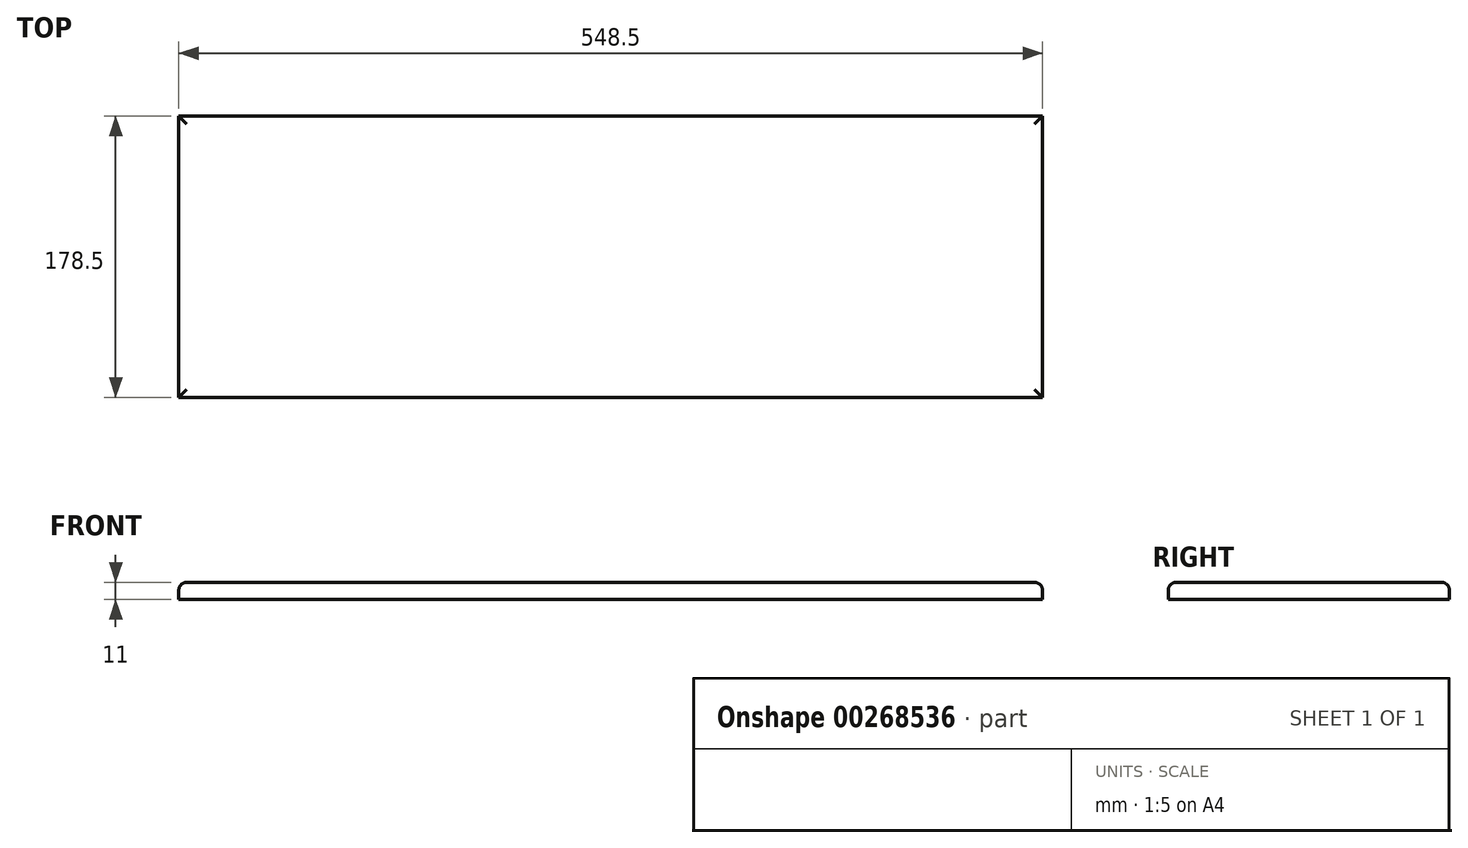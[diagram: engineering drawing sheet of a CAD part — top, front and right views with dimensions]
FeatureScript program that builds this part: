
annotation { "Feature Type Name" : "Feature", "Feature Type Description" : "" }
export const myFeature = defineFeature(function(context is Context, id is Id, definition is map)
    precondition{}
    {
        {
            var Q0;
            Q0=qCreatedBy(makeId("Top.planeOp"),FACE);
            var sketch = newSketch(context, id + "F0", { "sketchPlane" : qUnion([Q0])});
            skLineSegment(sketch, "E0.bottom", {"start": v(0, 0) * mm, "end": v(548.5, 0) * mm});
            skLineSegment(sketch, "E0.top", {"start": v(0, -178.5) * mm, "end": v(548.5, -178.5) * mm});
            skLineSegment(sketch, "E0.left", {"start": v(0, 0) * mm, "end": v(0, -178.5) * mm});
            skLineSegment(sketch, "E0.right", {"start": v(548.5, 0) * mm, "end": v(548.5, -178.5) * mm});
            skSolve(sketch);
        }
        {
            var Q0;
            Q0 = qSketchRegion(id + "F0", true);
            extrude(context, id + "F1", {"entities" : qUnion([Q0]), "depth" : 11 * mm});
        }
        {
            var Q0;
            Q0=makeQuery(id+"F1.opExtrude","CAP_EDGE",EDGE,{"disambiguationData":[OSD([sQuery(id+"F0.wireOp",EDGE,"E0.top")])],"isStart":false});
            var Q1;
            Q1=makeQuery(id+"F1.opExtrude","CAP_EDGE",EDGE,{"disambiguationData":[OSD([sQuery(id+"F0.wireOp",EDGE,"E0.left")])],"isStart":false});
            var Q2;
            Q2=makeQuery(id+"F1.opExtrude","CAP_EDGE",EDGE,{"disambiguationData":[OSD([sQuery(id+"F0.wireOp",EDGE,"E0.bottom")])],"isStart":false});
            var Q3;
            Q3=makeQuery(id+"F1.opExtrude","CAP_EDGE",EDGE,{"disambiguationData":[OSD([sQuery(id+"F0.wireOp",EDGE,"E0.right")])],"isStart":false});
            fillet(context, id + "F2", {"entities" : qUnion([Q0, Q1, Q2, Q3]), "radius" : 5 * mm, "tangentPropagation" : true, "allowEdgeOverflow" : false});
        }
    });
